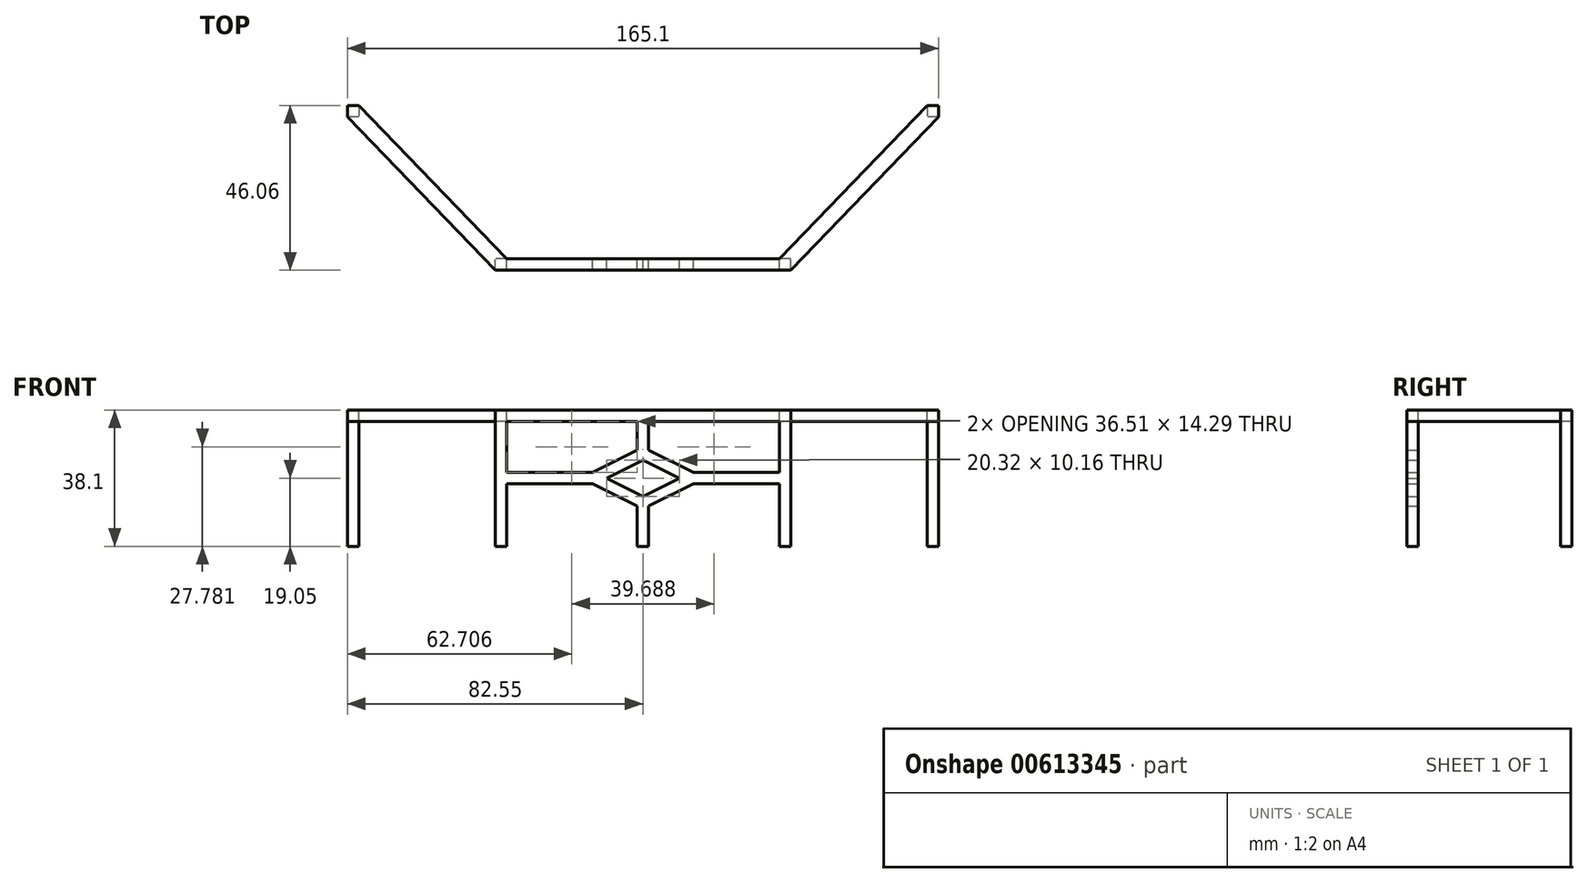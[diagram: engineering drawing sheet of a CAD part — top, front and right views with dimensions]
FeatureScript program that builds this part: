
annotation { "Feature Type Name" : "Feature", "Feature Type Description" : "" }
export const myFeature = defineFeature(function(context is Context, id is Id, definition is map)
    precondition{}
    {
        {
            var Q0;
            Q0=qCreatedBy(makeId("Front.planeOp"),FACE);
            var sketch = newSketch(context, id + "F0", { "sketchPlane" : qUnion([Q0])});
            skLineSegment(sketch, "E0.bottom", {"start": v(41.28, 19.05) * mm, "end": v(-41.28, 19.05) * mm});
            skLineSegment(sketch, "E0.top", {"start": v(41.28, -19.05) * mm, "end": v(38.1, -19.05) * mm});
            skLineSegment(sketch, "E0.left", {"start": v(41.28, 19.05) * mm, "end": v(41.28, -19.05) * mm});
            skLineSegment(sketch, "E0.right", {"start": v(-41.28, 19.05) * mm, "end": v(-41.27, -19.05) * mm});
            skPoint(sketch, "E0.middle", {"position": v(0, 0) * mm});
            skLineSegment(sketch, "E1.0", {"start": v(-38.1, 15.88) * mm, "end": v(-38.1, 1.59) * mm});
            skLineSegment(sketch, "E2.0", {"start": v(38.1, 15.88) * mm, "end": v(38.1, 1.59) * mm});
            skLineSegment(sketch, "E3.0", {"start": v(38.1, 15.88) * mm, "end": v(1.59, 15.88) * mm});
            skEllipse(sketch, "E4", {"center": v(0, 0) * mm, "majorRadius": 6.35 * mm, "minorRadius": 3.18 * mm, "majorAxis": v(1, 0)});
            skLineSegment(sketch, "E5.0", {"start": v(1.59, -19.05) * mm, "end": v(1.59, -7.84) * mm});
            skLineSegment(sketch, "E6.0", {"start": v(-1.59, -19.05) * mm, "end": v(-1.59, -7.84) * mm});
            skLineSegment(sketch, "E7.0", {"start": v(-38.1, -1.59) * mm, "end": v(-14.08, -1.59) * mm});
            skLineSegment(sketch, "E8.0", {"start": v(-38.1, 1.59) * mm, "end": v(-14.08, 1.59) * mm});
            skLineSegment(sketch, "E9", {"start": v(-10.16, 0) * mm, "end": v(0, 5.08) * mm});
            skLineSegment(sketch, "E10", {"start": v(-10.16, 0) * mm, "end": v(0, -5.08) * mm});
            skLineSegment(sketch, "E11", {"start": v(10.16, 0) * mm, "end": v(0, -5.08) * mm});
            skLineSegment(sketch, "E12", {"start": v(10.16, 0) * mm, "end": v(0, 5.08) * mm});
            skLineSegment(sketch, "E13.trimOffspring", {"start": v(14.08, -1.59) * mm, "end": v(38.1, -1.59) * mm});
            skLineSegment(sketch, "E14.trimOffspring", {"start": v(14.08, 1.59) * mm, "end": v(38.1, 1.59) * mm});
            skLineSegment(sketch, "E15.trimOffspring", {"start": v(-1.59, 7.84) * mm, "end": v(-1.59, 15.88) * mm});
            skLineSegment(sketch, "E16.trimOffspring", {"start": v(1.59, 7.84) * mm, "end": v(1.59, 15.88) * mm});
            skLineSegment(sketch, "E17.0", {"start": v(-14.08, 1.59) * mm, "end": v(-1.59, 7.84) * mm});
            skLineSegment(sketch, "E18.0", {"start": v(-14.08, -1.59) * mm, "end": v(-1.59, -7.84) * mm});
            skLineSegment(sketch, "E19.0", {"start": v(14.08, -1.59) * mm, "end": v(1.59, -7.84) * mm});
            skLineSegment(sketch, "E20.0", {"start": v(14.08, 1.59) * mm, "end": v(1.59, 7.84) * mm});
            skLineSegment(sketch, "E21.trimOffspring", {"start": v(-38.1, -1.59) * mm, "end": v(-38.1, -19.05) * mm});
            skLineSegment(sketch, "E22.trimOffspring", {"start": v(-1.59, 15.88) * mm, "end": v(-38.1, 15.88) * mm});
            skLineSegment(sketch, "E23.trimOffspring", {"start": v(38.1, -1.59) * mm, "end": v(38.1, -19.05) * mm});
            skLineSegment(sketch, "E24.trimOffspring", {"start": v(1.59, -19.05) * mm, "end": v(-1.59, -19.05) * mm});
            skLineSegment(sketch, "E25.trimOffspring", {"start": v(-38.1, -19.05) * mm, "end": v(-41.28, -19.05) * mm});
            skSolve(sketch);
        }
        {
            var Q0;
            Q0=makeQuery(id+"F0.imprint","IMPRINT",FACE,{"disambiguationData":[TD([[makeQuery(id+"F0.imprint","IMPRINT",EDGE,{"derivedFrom":sQuery(id+"F0.wireOp",EDGE,"E0.bottom")}),1.0]])]});
            extrude(context, id + "F1", {"entities" : qUnion([Q0]), "depth" : 3.17 * mm, "offsetDistance" : 25.4 * mm});
        }
        {
            var Q0;
            Q0=makeQuery(id+"F1.opExtrude","SWEPT_FACE",FACE,{"disambiguationData":[OSD([sQuery(id+"F0.wireOp",EDGE,"E0.bottom")])]});
            var sketch = newSketch(context, id + "F2", { "sketchPlane" : qUnion([Q0])});
            skLineSegment(sketch, "E26.bottom", {"start": v(-41.28, -3.18) * mm, "end": v(-38.1, -3.18) * mm});
            skLineSegment(sketch, "E26.top", {"start": v(-41.28, 0) * mm, "end": v(-38.1, 0) * mm});
            skLineSegment(sketch, "E26.left", {"start": v(-41.28, -3.18) * mm, "end": v(-41.28, 0) * mm});
            skLineSegment(sketch, "E26.right", {"start": v(-38.1, -3.18) * mm, "end": v(-38.1, 0) * mm});
            skLineSegment(sketch, "E27.bottom", {"start": v(41.28, -3.18) * mm, "end": v(38.1, -3.18) * mm});
            skLineSegment(sketch, "E27.top", {"start": v(41.28, 0) * mm, "end": v(38.1, 0) * mm});
            skLineSegment(sketch, "E27.left", {"start": v(41.28, -3.18) * mm, "end": v(41.28, 0) * mm});
            skLineSegment(sketch, "E27.right", {"start": v(38.1, -3.18) * mm, "end": v(38.1, 0) * mm});
            skPoint(sketch, "E28.startSnap0", {"position": v(-39.69, 0) * mm});
            skPoint(sketch, "E28.startSnap1", {"position": v(-41.28, -1.59) * mm});
            skLineSegment(sketch, "E29.bottom", {"start": v(-79.38, 42.88) * mm, "end": v(-82.55, 42.88) * mm});
            skLineSegment(sketch, "E29.top", {"start": v(-79.38, 39.7) * mm, "end": v(-82.55, 39.7) * mm});
            skLineSegment(sketch, "E29.left", {"start": v(-79.38, 42.88) * mm, "end": v(-79.38, 39.7) * mm});
            skLineSegment(sketch, "E29.right", {"start": v(-82.55, 42.88) * mm, "end": v(-82.55, 39.7) * mm});
            skPoint(sketch, "E29.middle", {"position": v(-80.96, 41.29) * mm});
            skLineSegment(sketch, "E30.bottom", {"start": v(82.55, 42.88) * mm, "end": v(79.37, 42.88) * mm});
            skLineSegment(sketch, "E30.top", {"start": v(82.55, 39.7) * mm, "end": v(79.37, 39.7) * mm});
            skLineSegment(sketch, "E30.left", {"start": v(82.55, 42.88) * mm, "end": v(82.55, 39.7) * mm});
            skLineSegment(sketch, "E30.right", {"start": v(79.37, 42.88) * mm, "end": v(79.37, 39.7) * mm});
            skPoint(sketch, "E30.middle", {"position": v(80.96, 41.29) * mm});
            skLineSegment(sketch, "E31", {"start": v(82.55, 39.7) * mm, "end": v(41.28, -3.17) * mm});
            skLineSegment(sketch, "E32", {"start": v(38.1, 0) * mm, "end": v(79.37, 42.88) * mm});
            skLineSegment(sketch, "E33", {"start": v(-38.1, 0) * mm, "end": v(-79.38, 42.88) * mm});
            skLineSegment(sketch, "E34", {"start": v(-82.55, 39.7) * mm, "end": v(-41.28, -3.18) * mm});
            skSolve(sketch);
        }
        {
            var Q0;
            Q0=makeQuery(id+"F2.imprint","IMPRINT",FACE,{"disambiguationData":[TD([[makeQuery(id+"F2.imprint","IMPRINT",EDGE,{"derivedFrom":sQuery(id+"F2.wireOp",EDGE,"E26.top")}),-1.0]])]});
            var Q1;
            Q1=makeQuery(id+"F2.imprint","IMPRINT",FACE,{"disambiguationData":[TD([[makeQuery(id+"F2.imprint","IMPRINT",EDGE,{"derivedFrom":sQuery(id+"F2.wireOp",EDGE,"E27.top")}),-1.0]])]});
            extrude(context, id + "F3", {"entities" : qUnion([Q0, Q1]), "operationType" : NewBodyOperationType.ADD, "oppositeDirection" : true, "depth" : 3.17 * mm, "offsetDistance" : 25.4 * mm});
        }
        {
            var Q0;
            Q0=makeQuery(id+"F3.boolean.opBoolean","MERGE",FACE,{"derivedFrom":[makeQuery(id+"F1.opExtrude","SWEPT_FACE",FACE,{"disambiguationData":[OSD([sQuery(id+"F0.wireOp",EDGE,"E0.bottom")])]}),makeQuery(id+"F3.opExtrude","CAP_FACE",FACE,{"disambiguationData":[OSD([sQuery(id+"F2.wireOp",EDGE,"E26.top"),sQuery(id+"F2.wireOp",EDGE,"E26.left"),sQuery(id+"F2.wireOp",EDGE,"E29.top"),sQuery(id+"F2.wireOp",EDGE,"E29.left"),sQuery(id+"F2.wireOp",EDGE,"E33"),sQuery(id+"F2.wireOp",EDGE,"E34")])],"isStart":true}),makeQuery(id+"F3.opExtrude","CAP_FACE",FACE,{"disambiguationData":[OSD([sQuery(id+"F2.wireOp",EDGE,"E27.top"),sQuery(id+"F2.wireOp",EDGE,"E27.left"),sQuery(id+"F2.wireOp",EDGE,"E30.top"),sQuery(id+"F2.wireOp",EDGE,"E30.right"),sQuery(id+"F2.wireOp",EDGE,"E31"),sQuery(id+"F2.wireOp",EDGE,"E32")])],"isStart":true})]});
            var sketch = newSketch(context, id + "F4", { "sketchPlane" : qUnion([Q0])});
            skLineSegment(sketch, "E35.bottom", {"start": v(-82.55, 39.7) * mm, "end": v(-79.38, 39.7) * mm});
            skLineSegment(sketch, "E35.top", {"start": v(-82.55, 42.88) * mm, "end": v(-79.38, 42.88) * mm});
            skLineSegment(sketch, "E35.left", {"start": v(-82.55, 39.7) * mm, "end": v(-82.55, 42.88) * mm});
            skLineSegment(sketch, "E35.right", {"start": v(-79.38, 39.7) * mm, "end": v(-79.38, 42.88) * mm});
            skLineSegment(sketch, "E36.bottom", {"start": v(82.55, 39.7) * mm, "end": v(79.37, 39.7) * mm});
            skLineSegment(sketch, "E36.top", {"start": v(82.55, 42.88) * mm, "end": v(79.37, 42.88) * mm});
            skLineSegment(sketch, "E36.left", {"start": v(82.55, 39.7) * mm, "end": v(82.55, 42.88) * mm});
            skLineSegment(sketch, "E36.right", {"start": v(79.37, 39.7) * mm, "end": v(79.37, 42.88) * mm});
            skSolve(sketch);
        }
        {
            var Q0;
            Q0=makeQuery(id+"F4.imprint","IMPRINT",FACE,{"disambiguationData":[TD([[makeQuery(id+"F4.imprint","IMPRINT",EDGE,{"derivedFrom":sQuery(id+"F4.wireOp",EDGE,"E35.bottom")}),-1.0]])]});
            var Q1;
            Q1=makeQuery(id+"F4.imprint","IMPRINT",FACE,{"disambiguationData":[TD([[makeQuery(id+"F4.imprint","IMPRINT",EDGE,{"derivedFrom":sQuery(id+"F4.wireOp",EDGE,"E36.bottom")}),-1.0]])]});
            extrude(context, id + "F5", {"entities" : qUnion([Q0, Q1]), "operationType" : NewBodyOperationType.ADD, "oppositeDirection" : true, "depth" : 38.1 * mm, "offsetDistance" : 25.4 * mm});
        }
    });
